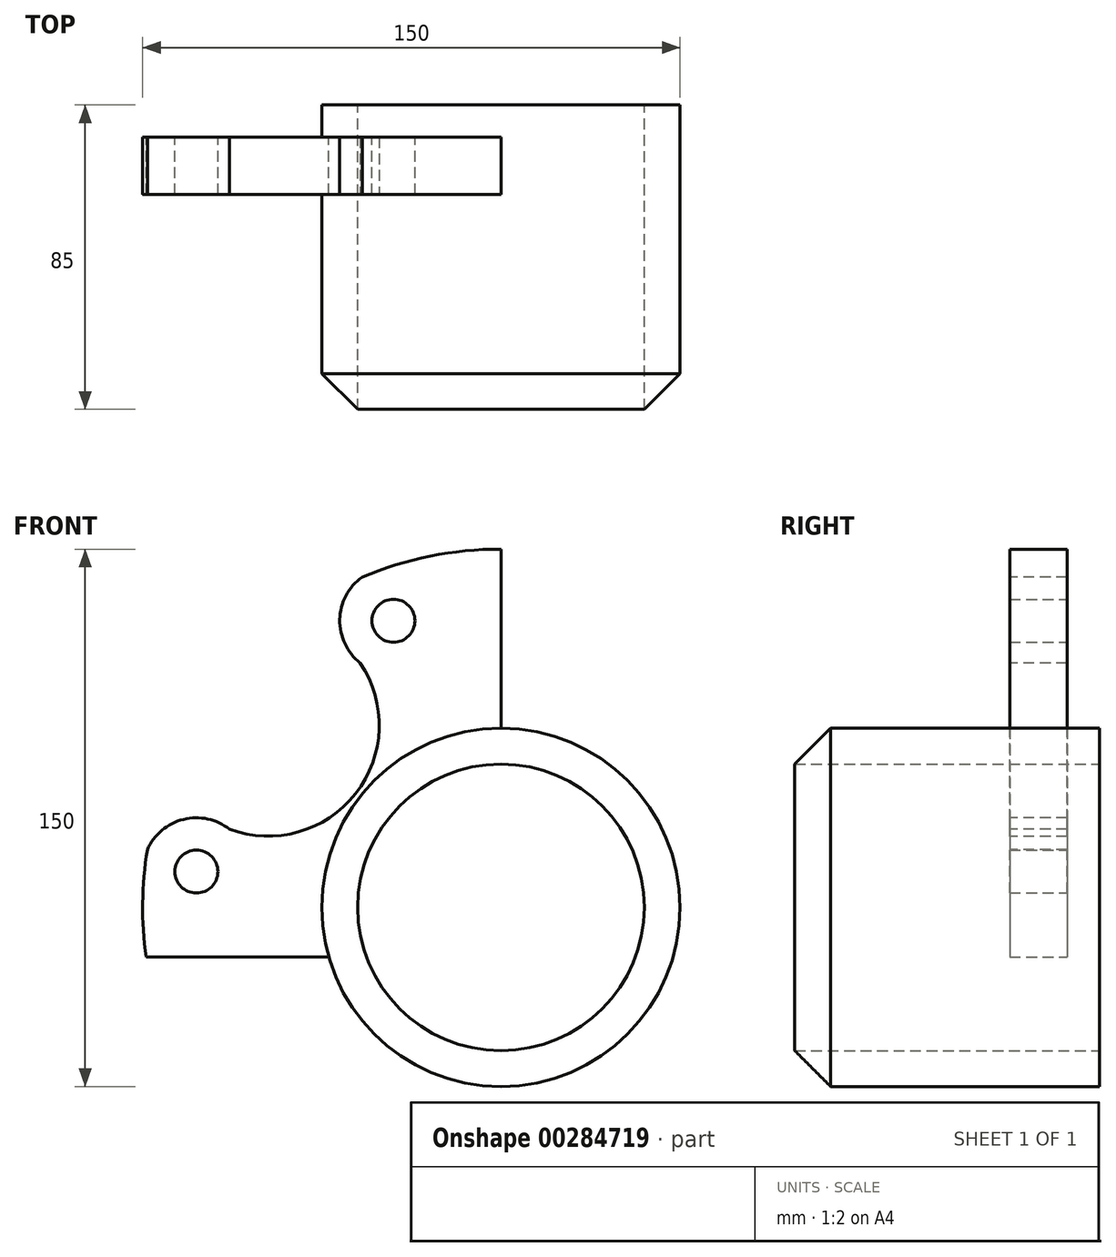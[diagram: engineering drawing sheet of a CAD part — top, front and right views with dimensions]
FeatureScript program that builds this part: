
annotation { "Feature Type Name" : "Feature", "Feature Type Description" : "" }
export const myFeature = defineFeature(function(context is Context, id is Id, definition is map)
    precondition{}
    {
        {
            var Q0;
            Q0=qCreatedBy(makeId("Front.planeOp"),FACE);
            var sketch = newSketch(context, id + "F0", { "sketchPlane" : qUnion([Q0])});
            skCircle(sketch, "E0", {"center": v(0, 0) * mm, "radius": 50 * mm});
            skCircle(sketch, "E1", {"center": v(0, 0) * mm, "radius": 40 * mm});
            skSolve(sketch);
        }
        {
            var Q0;
            Q0=qSketchRegion(id+"F0",true);
            extrude(context, id + "F1", {"entities" : qUnion([Q0]), "depth" : 85 * mm});
        }
        {
            var Q0;
            Q0=qCreatedBy(makeId("Front.planeOp"),FACE);
            cPlane(context, id + "F2", {"entities" : qUnion([Q0]), "cplaneType" : CPlaneType.OFFSET, "offset" : 9 * mm, "width" : 150 * mm, "height" : 150 * mm});
        }
        {
            var Q0;
            Q0=qCreatedBy(id+"F2.planeOp",FACE);
            var sketch = newSketch(context, id + "F3", { "sketchPlane" : qUnion([Q0])});
            skCircle(sketch, "E2.0", {"center": v(0, 0) * mm, "radius": 50 * mm});
            skArc(sketch, "E3", {"start": v(0, 100) * mm, "mid": v(-75.46, 65.61) * mm, "end": v(-99.03, -13.9) * mm});
            skLineSegment(sketch, "E4", {"start": v(0, 50) * mm, "end": v(0, 100) * mm});
            skLineSegment(sketch, "E5", {"start": v(-48.03, -13.9) * mm, "end": v(-99.03, -13.9) * mm});
            skSolve(sketch);
        }
        {
            var Q0;
            Q0=makeQuery(id+"F3.imprint","IMPRINT",FACE,{"disambiguationData":[TD([[makeQuery(id+"F3.imprint","IMPRINT",EDGE,{"derivedFrom":sQuery(id+"F3.wireOp",EDGE,"E3")}),1.0]])]});
            extrude(context, id + "F4", {"entities" : qUnion([Q0]), "operationType" : NewBodyOperationType.ADD, "depth" : 16 * mm});
        }
        {
            var Q0;
            Q0=qCreatedBy(id+"F2.planeOp",FACE);
            var sketch = newSketch(context, id + "F5", { "sketchPlane" : qUnion([Q0])});
            skLineSegment(sketch, "E6", {"start": v(0, 0) * mm, "end": v(0, 80) * mm, "construction": true});
            skLineSegment(sketch, "E7", {"start": v(0, 80) * mm, "end": v(-30, 80) * mm, "construction": true});
            skLineSegment(sketch, "E8", {"start": v(0, 0) * mm, "end": v(-85, 0) * mm, "construction": true});
            skLineSegment(sketch, "E9", {"start": v(-85, 0) * mm, "end": v(-85, 10) * mm, "construction": true});
            skLineSegment(sketch, "E10", {"start": v(-85, 10) * mm, "end": v(0, 0) * mm});
            skLineSegment(sketch, "E11", {"start": v(-30, 80) * mm, "end": v(0, 0) * mm});
            skCircle(sketch, "E12", {"center": v(-30, 80) * mm, "radius": 6 * mm});
            skCircle(sketch, "E13", {"center": v(-85, 10) * mm, "radius": 6 * mm});
            skSolve(sketch);
        }
        {
            var Q0;
            Q0=qSketchRegion(id+"F5",true);
            extrude(context, id + "F6", {"entities" : qUnion([Q0]), "operationType" : NewBodyOperationType.REMOVE, "depth" : 18 * mm});
        }
        {
            var Q0;
            {var subQ0=sQuery(id+"F3.wireOp",EDGE,"GF1FPOM8-uyVP-Hu2m-4zos-hD67tdTqi4Pm");var subQ1=sQuery(id+"F3.wireOp",EDGE,"obdFilX4-0A2j-ghXX-8LBF-lPKM0k6eU9od");var subQ2=sQuery(id+"F3.wireOp",EDGE,"tjBiYEB3-9Sjd-J6s2-U4cC-OyrZbL43CpGe");Q0=makeQuery(id+"F4.boolean.opBoolean","SPLIT",FACE,{"disambiguationData":[TD([makeQuery(id+"F1.opExtrude","SWEPT_FACE",FACE,{"disambiguationData":[OSD([sQuery(id+"F0.wireOp",EDGE,"E0")])]})])],"derivedFrom":makeQuery(id+"F4.opExtrude","CAP_FACE",FACE,{"disambiguationData":[OSD([subQ0,sQuery(id+"F3.wireOp",EDGE,"E2.0"),subQ1,subQ2])],"isStart":false})});}
            var sketch = newSketch(context, id + "F7", { "sketchPlane" : qUnion([Q0])});
            skCircle(sketch, "E14.0", {"center": v(-30, 80) * mm, "radius": 6 * mm});
            skCircle(sketch, "E15", {"center": v(-30, 80) * mm, "radius": 15 * mm});
            skCircle(sketch, "E16.1", {"center": v(-85, 10) * mm, "radius": 6 * mm});
            skCircle(sketch, "E17", {"center": v(-85, 10) * mm, "radius": 15 * mm});
            skLineSegment(sketch, "E18", {"start": v(-30, 80) * mm, "end": v(-85, 10) * mm, "construction": true});
            skArc(sketch, "E19", {"start": v(-75.73, 21.8) * mm, "mid": v(-40.59, 31.71) * mm, "end": v(-39.27, 68.2) * mm});
            skSolve(sketch);
        }
        {
            var Q0;
            {var subQ0=sQuery(id+"F7.wireOp",EDGE,"E15");var subQ1=makeQuery(id+"F4.opExtrude","CAP_EDGE",EDGE,{"disambiguationData":[OSD([sQuery(id+"F3.wireOp",EDGE,"E3")])],"isStart":false});var subQ2=makeQuery(id+"F7.imprint","INTERSECT",VERTEX,{"disambiguationData":[OD(0.0)],"derivedFrom":[subQ1,subQ0]});Q0=makeQuery(id+"F7.imprint","IMPRINT",FACE,{"disambiguationData":[TD([[makeQuery(id+"F7.imprint","IMPRINT",EDGE,{"disambiguationData":[TD([[subQ2,1.0]])],"derivedFrom":subQ0}),1.0]])]});}
            var Q1;
            {var subQ0=sQuery(id+"F7.wireOp",EDGE,"E17");var subQ1=makeQuery(id+"F4.opExtrude","CAP_EDGE",EDGE,{"disambiguationData":[OSD([sQuery(id+"F3.wireOp",EDGE,"E3")])],"isStart":false});var subQ2=makeQuery(id+"F7.imprint","INTERSECT",VERTEX,{"disambiguationData":[OD(0.0)],"derivedFrom":[subQ1,subQ0]});Q1=makeQuery(id+"F7.imprint","IMPRINT",FACE,{"disambiguationData":[TD([[makeQuery(id+"F7.imprint","IMPRINT",EDGE,{"disambiguationData":[TD([[subQ2,-1.0]])],"derivedFrom":subQ0}),1.0]])]});}
            var Q2;
            {var subQ0=sQuery(id+"F7.wireOp",EDGE,"KmoiiIbb-Bgaa-k1dx-24Oj-8pEW61p2rezh");var subQ1=sQuery(id+"F7.wireOp",EDGE,"E15");var subQ2=makeQuery(id+"F7.imprint","INTERSECT",VERTEX,{"derivedFrom":[subQ1,subQ0]});Q2=makeQuery(id+"F7.imprint","IMPRINT",FACE,{"disambiguationData":[TD([[makeQuery(id+"F7.imprint","IMPRINT",EDGE,{"disambiguationData":[TD([[subQ2,1.0]])],"derivedFrom":subQ1}),-1.0]])]});}
            extrude(context, id + "F8", {"entities" : qUnion([Q0, Q1, Q2]), "operationType" : NewBodyOperationType.REMOVE, "oppositeDirection" : true, "depth" : 17 * mm});
        }
        {
            var Q0;
            Q0=makeQuery(id+"F1.opExtrude","CAP_EDGE",EDGE,{"disambiguationData":[OSD([sQuery(id+"F0.wireOp",EDGE,"E0")])],"isStart":false});
            chamfer(context, id + "F9", {"entities" : qUnion([Q0]), "width" : 10 * mm, "tangentPropagation" : true});
        }
    });
